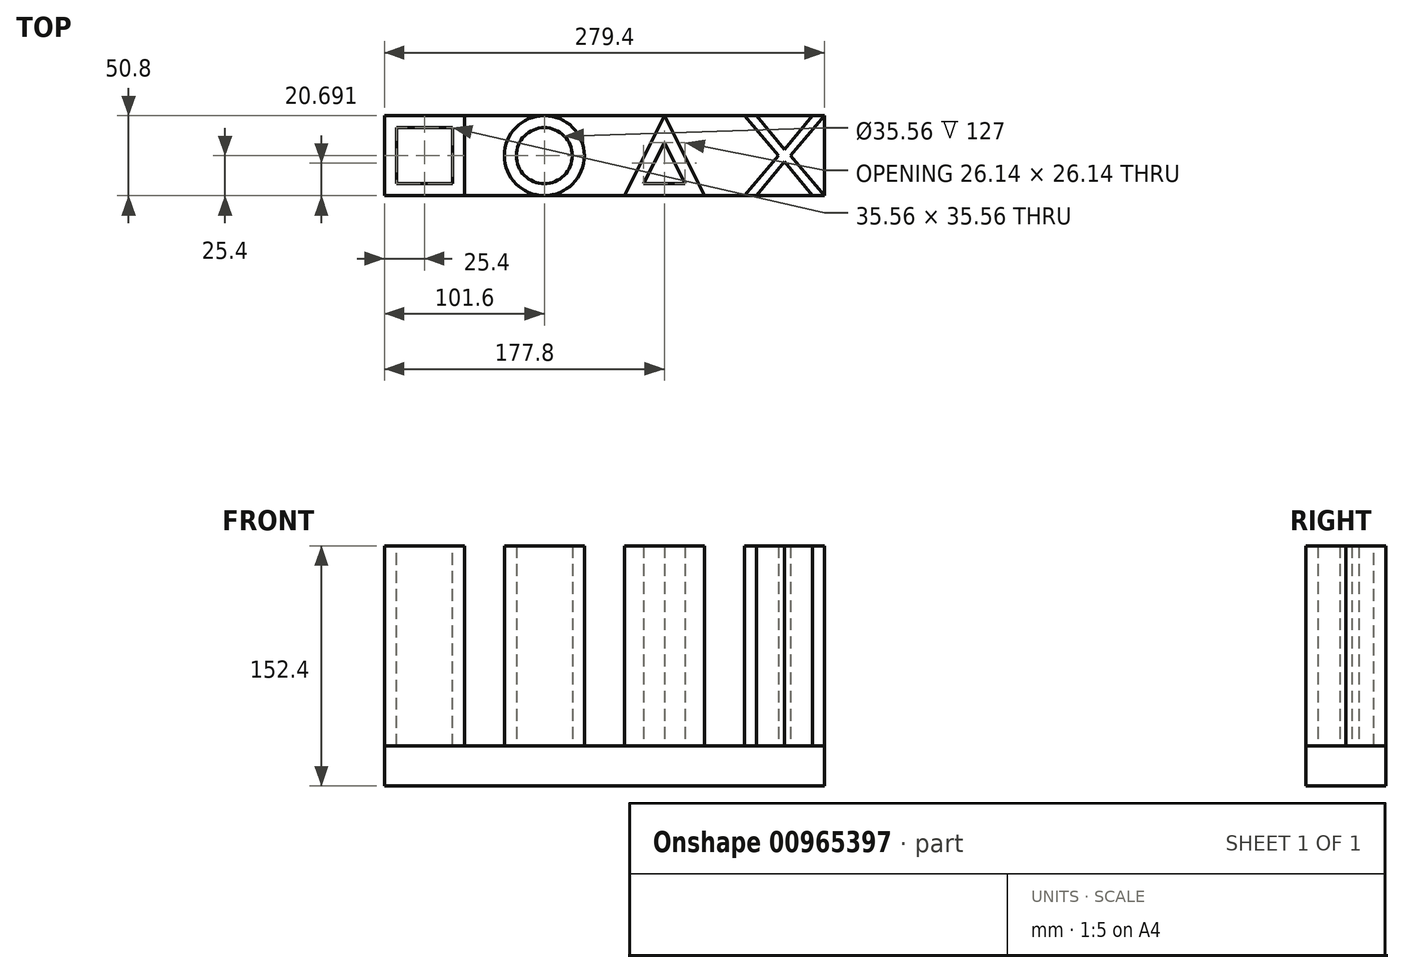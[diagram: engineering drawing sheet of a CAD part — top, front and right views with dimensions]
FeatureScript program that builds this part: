
annotation { "Feature Type Name" : "Feature", "Feature Type Description" : "" }
export const myFeature = defineFeature(function(context is Context, id is Id, definition is map)
    precondition{}
    {
        {
            var Q0;
            Q0=qCreatedBy(makeId("Top.planeOp"),FACE);
            var sketch = newSketch(context, id + "F0", { "sketchPlane" : qUnion([Q0])});
            skLineSegment(sketch, "E0.bottom", {"start": v(139.7, -25.4) * mm, "end": v(-139.7, -25.4) * mm});
            skLineSegment(sketch, "E0.top", {"start": v(139.7, 25.4) * mm, "end": v(-139.7, 25.4) * mm});
            skLineSegment(sketch, "E0.left", {"start": v(139.7, -25.4) * mm, "end": v(139.7, 25.4) * mm});
            skLineSegment(sketch, "E0.right", {"start": v(-139.7, -25.4) * mm, "end": v(-139.7, 25.4) * mm});
            skPoint(sketch, "E0.middle", {"position": v(0, 0) * mm});
            skSolve(sketch);
        }
        {
            var Q0;
            Q0 = qSketchRegion(id + "F0", true);
            extrude(context, id + "F1", {"entities" : qUnion([Q0]), "oppositeDirection" : true, "depth" : 25.4 * mm, "offsetDistance" : 25.4 * mm});
        }
        {
            var Q0;
            Q0=makeQuery(id+"F1.opExtrude","CAP_FACE",FACE,{"disambiguationData":[OSD([sQuery(id+"F0.wireOp",EDGE,"E0.bottom"),sQuery(id+"F0.wireOp",EDGE,"E0.top"),sQuery(id+"F0.wireOp",EDGE,"E0.left"),sQuery(id+"F0.wireOp",EDGE,"E0.right")])],"isStart":true});
            var sketch = newSketch(context, id + "F2", { "sketchPlane" : qUnion([Q0])});
            skLineSegment(sketch, "E1.bottom", {"start": v(-139.7, 25.4) * mm, "end": v(-88.9, 25.4) * mm});
            skLineSegment(sketch, "E1.top", {"start": v(-139.7, -25.4) * mm, "end": v(-88.9, -25.4) * mm});
            skLineSegment(sketch, "E1.left", {"start": v(-139.7, 25.4) * mm, "end": v(-139.7, -25.4) * mm});
            skLineSegment(sketch, "E1.right", {"start": v(-88.9, 25.4) * mm, "end": v(-88.9, -25.4) * mm});
            skSolve(sketch);
        }
        {
            var Q0;
            Q0 = qSketchRegion(id + "F2", true);
            extrude(context, id + "F3", {"entities" : qUnion([Q0]), "depth" : 127 * mm, "offsetDistance" : 25.4 * mm});
        }
        {
            var Q0;
            Q0=makeQuery(id+"F3.opExtrude","CAP_FACE",FACE,{"disambiguationData":[OSD([sQuery(id+"F2.wireOp",EDGE,"E1.bottom"),sQuery(id+"F2.wireOp",EDGE,"E1.top"),sQuery(id+"F2.wireOp",EDGE,"E1.left"),sQuery(id+"F2.wireOp",EDGE,"E1.right")])],"isStart":false});
            var sketch = newSketch(context, id + "F4", { "sketchPlane" : qUnion([Q0])});
            skLineSegment(sketch, "E2.bottom", {"start": v(-132.08, -17.78) * mm, "end": v(-96.52, -17.78) * mm});
            skLineSegment(sketch, "E2.top", {"start": v(-132.08, 17.78) * mm, "end": v(-96.52, 17.78) * mm});
            skLineSegment(sketch, "E2.left", {"start": v(-132.08, -17.78) * mm, "end": v(-132.08, 17.78) * mm});
            skLineSegment(sketch, "E2.right", {"start": v(-96.52, -17.78) * mm, "end": v(-96.52, 17.78) * mm});
            skPoint(sketch, "E2.middle", {"position": v(-114.3, 0) * mm});
            skPoint(sketch, "E2.middle.positionSnap0", {"position": v(-88.9, 0) * mm});
            skPoint(sketch, "E2.middle.positionSnap1", {"position": v(-114.3, 25.4) * mm});
            skPoint(sketch, "E2.centerSnap0", {"position": v(-88.9, 0) * mm});
            skPoint(sketch, "E2.centerSnap1", {"position": v(-114.3, 25.4) * mm});
            skSolve(sketch);
        }
        {
            var Q0;
            Q0 = qSketchRegion(id + "F4", true);
            extrude(context, id + "F5", {"entities" : qUnion([Q0]), "operationType" : NewBodyOperationType.REMOVE, "oppositeDirection" : true, "depth" : 127 * mm, "offsetDistance" : 25.4 * mm});
        }
        {
            var Q0;
            Q0=makeQuery(id+"F1.opExtrude","CAP_FACE",FACE,{"disambiguationData":[OSD([sQuery(id+"F0.wireOp",EDGE,"E0.bottom"),sQuery(id+"F0.wireOp",EDGE,"E0.top"),sQuery(id+"F0.wireOp",EDGE,"E0.left"),sQuery(id+"F0.wireOp",EDGE,"E0.right")])],"isStart":true});
            var sketch = newSketch(context, id + "F6", { "sketchPlane" : qUnion([Q0])});
            skCircle(sketch, "E3", {"center": v(-38.1, 0) * mm, "radius": 25.4 * mm});
            skCircle(sketch, "E4", {"center": v(-38.1, 0) * mm, "radius": 17.78 * mm});
            skSolve(sketch);
        }
        {
            var Q0;
            Q0 = qSketchRegion(id + "F6", true);
            extrude(context, id + "F7", {"entities" : qUnion([Q0]), "depth" : 127 * mm, "offsetDistance" : 25.4 * mm});
        }
        {
            var Q0;
            Q0=makeQuery(id+"F1.opExtrude","CAP_FACE",FACE,{"disambiguationData":[OSD([sQuery(id+"F0.wireOp",EDGE,"E0.bottom"),sQuery(id+"F0.wireOp",EDGE,"E0.top"),sQuery(id+"F0.wireOp",EDGE,"E0.left"),sQuery(id+"F0.wireOp",EDGE,"E0.right")])],"isStart":true});
            var sketch = newSketch(context, id + "F8", { "sketchPlane" : qUnion([Q0])});
            skLineSegment(sketch, "E5.bottom", {"start": v(12.7, -25.4) * mm, "end": v(63.5, -25.4) * mm});
            skLineSegment(sketch, "E6", {"start": v(38.1, 25.4) * mm, "end": v(12.7, -25.4) * mm});
            skLineSegment(sketch, "E7", {"start": v(38.1, 25.4) * mm, "end": v(63.5, -25.4) * mm});
            skLineSegment(sketch, "E8", {"start": v(38.1, 8.36) * mm, "end": v(25.03, -17.78) * mm});
            skLineSegment(sketch, "E9", {"start": v(25.03, -17.78) * mm, "end": v(51.17, -17.78) * mm});
            skLineSegment(sketch, "E10", {"start": v(51.17, -17.78) * mm, "end": v(38.1, 8.36) * mm});
            skSolve(sketch);
        }
        {
            var Q0;
            Q0 = qSketchRegion(id + "F8", true);
            extrude(context, id + "F9", {"entities" : qUnion([Q0]), "depth" : 127 * mm, "offsetDistance" : 25.4 * mm});
        }
        {
            var Q0;
            Q0=makeQuery(id+"F1.opExtrude","CAP_FACE",FACE,{"disambiguationData":[OSD([sQuery(id+"F0.wireOp",EDGE,"E0.bottom"),sQuery(id+"F0.wireOp",EDGE,"E0.top"),sQuery(id+"F0.wireOp",EDGE,"E0.left"),sQuery(id+"F0.wireOp",EDGE,"E0.right")])],"isStart":true});
            var sketch = newSketch(context, id + "F10", { "sketchPlane" : qUnion([Q0])});
            skPoint(sketch, "E11.middle", {"position": v(114.3, 0) * mm});
            skLineSegment(sketch, "E12", {"start": v(88.9, -25.4) * mm, "end": v(96.52, -25.4) * mm});
            skLineSegment(sketch, "E13", {"start": v(96.52, -25.4) * mm, "end": v(114.3, -3.81) * mm});
            skLineSegment(sketch, "E14", {"start": v(88.9, -25.4) * mm, "end": v(110.49, 0) * mm});
            skLineSegment(sketch, "E15", {"start": v(110.49, 0) * mm, "end": v(88.9, 25.4) * mm});
            skLineSegment(sketch, "E16", {"start": v(88.9, 25.4) * mm, "end": v(96.52, 25.4) * mm});
            skLineSegment(sketch, "E17", {"start": v(96.52, 25.4) * mm, "end": v(114.3, 3.8) * mm});
            skLineSegment(sketch, "E18", {"start": v(139.7, 25.4) * mm, "end": v(118.11, 0) * mm});
            skLineSegment(sketch, "E19", {"start": v(118.1, 0) * mm, "end": v(139.7, -25.4) * mm});
            skLineSegment(sketch, "E20", {"start": v(139.7, 25.4) * mm, "end": v(132.08, 25.4) * mm});
            skLineSegment(sketch, "E21", {"start": v(132.08, 25.4) * mm, "end": v(114.3, 3.8) * mm});
            skLineSegment(sketch, "E22", {"start": v(139.7, -25.4) * mm, "end": v(132.08, -25.4) * mm});
            skLineSegment(sketch, "E23", {"start": v(132.08, -25.4) * mm, "end": v(114.3, -3.81) * mm});
            skSolve(sketch);
        }
        {
            var Q0;
            Q0 = qSketchRegion(id + "F10", true);
            extrude(context, id + "F11", {"entities" : qUnion([Q0]), "depth" : 127 * mm, "offsetDistance" : 25.4 * mm});
        }
    });
